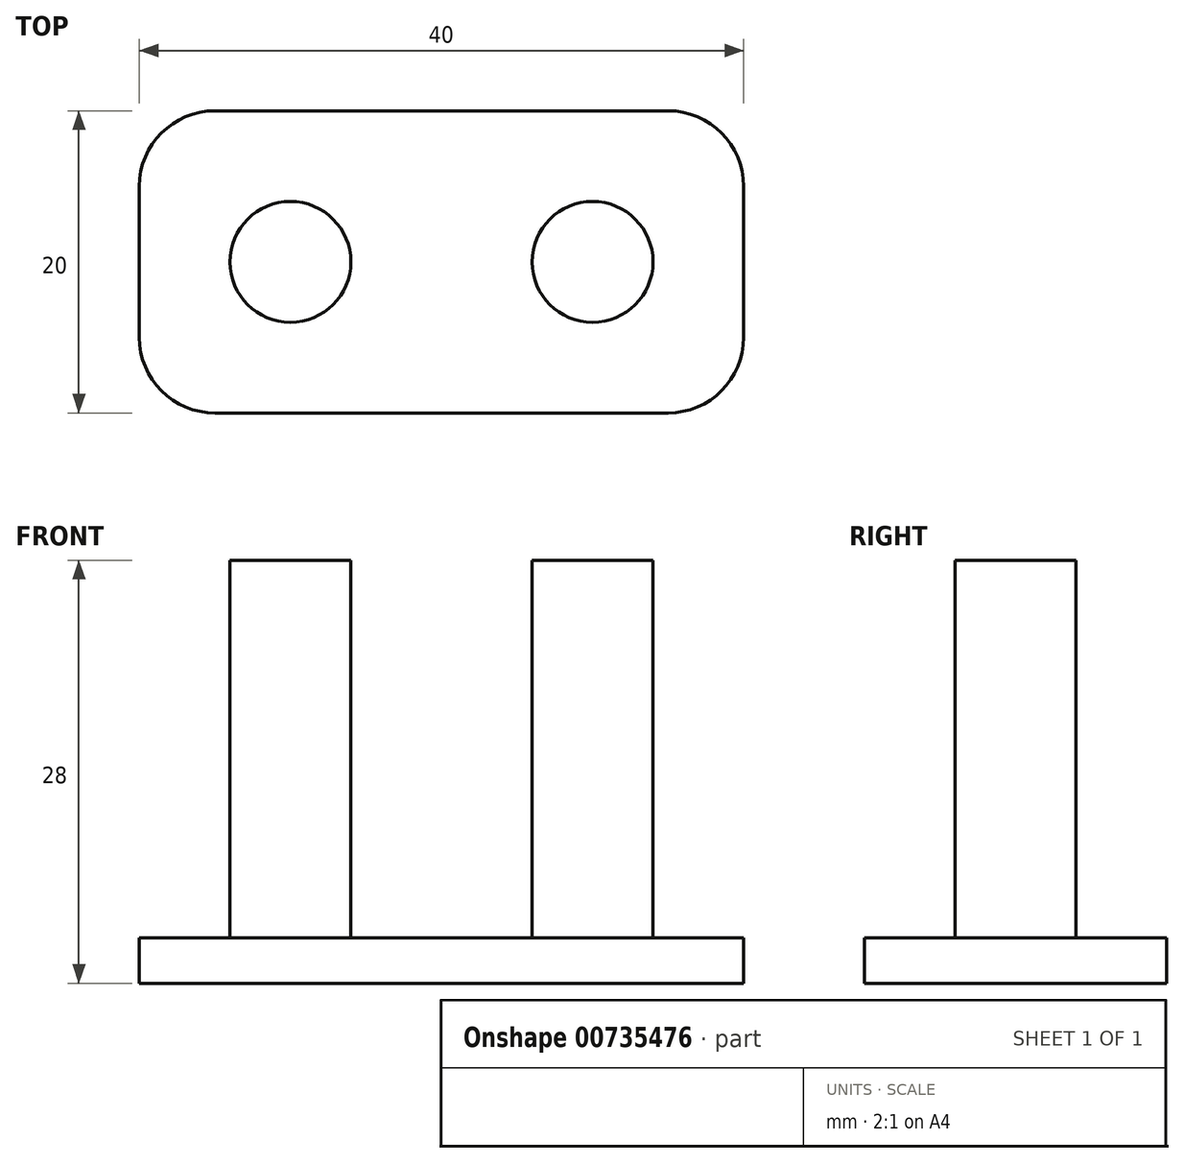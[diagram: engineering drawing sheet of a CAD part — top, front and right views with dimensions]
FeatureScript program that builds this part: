
annotation { "Feature Type Name" : "Feature", "Feature Type Description" : "" }
export const myFeature = defineFeature(function(context is Context, id is Id, definition is map)
    precondition{}
    {
        {
            var Q0;
            Q0=qCreatedBy(makeId("Top.planeOp"),FACE);
            var sketch = newSketch(context, id + "F0", { "sketchPlane" : qUnion([Q0])});
            skLineSegment(sketch, "E0.bottom", {"start": v(-20, 10) * mm, "end": v(20, 10) * mm});
            skLineSegment(sketch, "E0.top", {"start": v(-20, -10) * mm, "end": v(20, -10) * mm});
            skLineSegment(sketch, "E0.left", {"start": v(-20, 10) * mm, "end": v(-20, -10) * mm});
            skLineSegment(sketch, "E0.right", {"start": v(20, 10) * mm, "end": v(20, -10) * mm});
            skCircle(sketch, "E1", {"center": v(-10, 0) * mm, "radius": 4 * mm});
            skCircle(sketch, "E2", {"center": v(10, 0) * mm, "radius": 4 * mm});
            skSolve(sketch);
        }
        {
            var Q0;
            Q0=makeQuery(id+"F0.imprint","IMPRINT",FACE,{"disambiguationData":[TD([[makeQuery(id+"F0.imprint","IMPRINT",EDGE,{"derivedFrom":sQuery(id+"F0.wireOp",EDGE,"E0.bottom")}),-1.0]])]});
            var Q1;
            Q1=makeQuery(id+"F0.imprint","IMPRINT",FACE,{"disambiguationData":[TD([[makeQuery(id+"F0.imprint","IMPRINT",EDGE,{"derivedFrom":sQuery(id+"F0.wireOp",EDGE,"E1")}),1.0]])]});
            var Q2;
            Q2=makeQuery(id+"F0.imprint","IMPRINT",FACE,{"disambiguationData":[TD([[makeQuery(id+"F0.imprint","IMPRINT",EDGE,{"derivedFrom":sQuery(id+"F0.wireOp",EDGE,"E2")}),1.0]])]});
            extrude(context, id + "F1", {"entities" : qUnion([Q0, Q1, Q2]), "oppositeDirection" : true, "depth" : 3 * mm, "offsetDistance" : 25 * mm});
        }
        {
            var Q0;
            Q0=makeQuery(id+"F1.opExtrude","CAP_FACE",FACE,{"disambiguationData":[OSD([sQuery(id+"F0.wireOp",EDGE,"E0.bottom"),sQuery(id+"F0.wireOp",EDGE,"E0.top"),sQuery(id+"F0.wireOp",EDGE,"E0.left"),sQuery(id+"F0.wireOp",EDGE,"E0.right")])],"isStart":true});
            var sketch = newSketch(context, id + "F2", { "sketchPlane" : qUnion([Q0])});
            skCircle(sketch, "E3", {"center": v(-10, 0) * mm, "radius": 4 * mm});
            skCircle(sketch, "E4", {"center": v(10, 0) * mm, "radius": 4 * mm});
            skSolve(sketch);
        }
        {
            var Q0;
            Q0=makeQuery(id+"F2.imprint","IMPRINT",FACE,{"disambiguationData":[TD([[makeQuery(id+"F2.imprint","IMPRINT",EDGE,{"derivedFrom":sQuery(id+"F2.wireOp",EDGE,"E3")}),1.0]])]});
            var Q1;
            Q1=makeQuery(id+"F2.imprint","IMPRINT",FACE,{"disambiguationData":[TD([[makeQuery(id+"F2.imprint","IMPRINT",EDGE,{"derivedFrom":sQuery(id+"F2.wireOp",EDGE,"E4")}),1.0]])]});
            extrude(context, id + "F3", {"entities" : qUnion([Q0, Q1]), "operationType" : NewBodyOperationType.ADD, "depth" : 25 * mm, "offsetDistance" : 25 * mm});
        }
        {
            var Q0;
            Q0=makeQuery(id+"F1.opExtrude","SWEPT_EDGE",EDGE,{"disambiguationData":[OSD([sQuery(id+"F0.wireOp",EDGE,"E0.top"),sQuery(id+"F0.wireOp",EDGE,"E0.left")])]});
            var Q1;
            Q1=makeQuery(id+"F1.opExtrude","SWEPT_EDGE",EDGE,{"disambiguationData":[OSD([sQuery(id+"F0.wireOp",EDGE,"E0.bottom"),sQuery(id+"F0.wireOp",EDGE,"E0.left")])]});
            var Q2;
            Q2=makeQuery(id+"F1.opExtrude","SWEPT_EDGE",EDGE,{"disambiguationData":[OSD([sQuery(id+"F0.wireOp",EDGE,"E0.bottom"),sQuery(id+"F0.wireOp",EDGE,"E0.right")])]});
            var Q3;
            Q3=makeQuery(id+"F1.opExtrude","SWEPT_EDGE",EDGE,{"disambiguationData":[OSD([sQuery(id+"F0.wireOp",EDGE,"E0.top"),sQuery(id+"F0.wireOp",EDGE,"E0.right")])]});
            fillet(context, id + "F4", {"entities" : qUnion([Q0, Q1, Q2, Q3]), "radius" : 5 * mm, "tangentPropagation" : true, "allowEdgeOverflow" : false});
        }
    });
